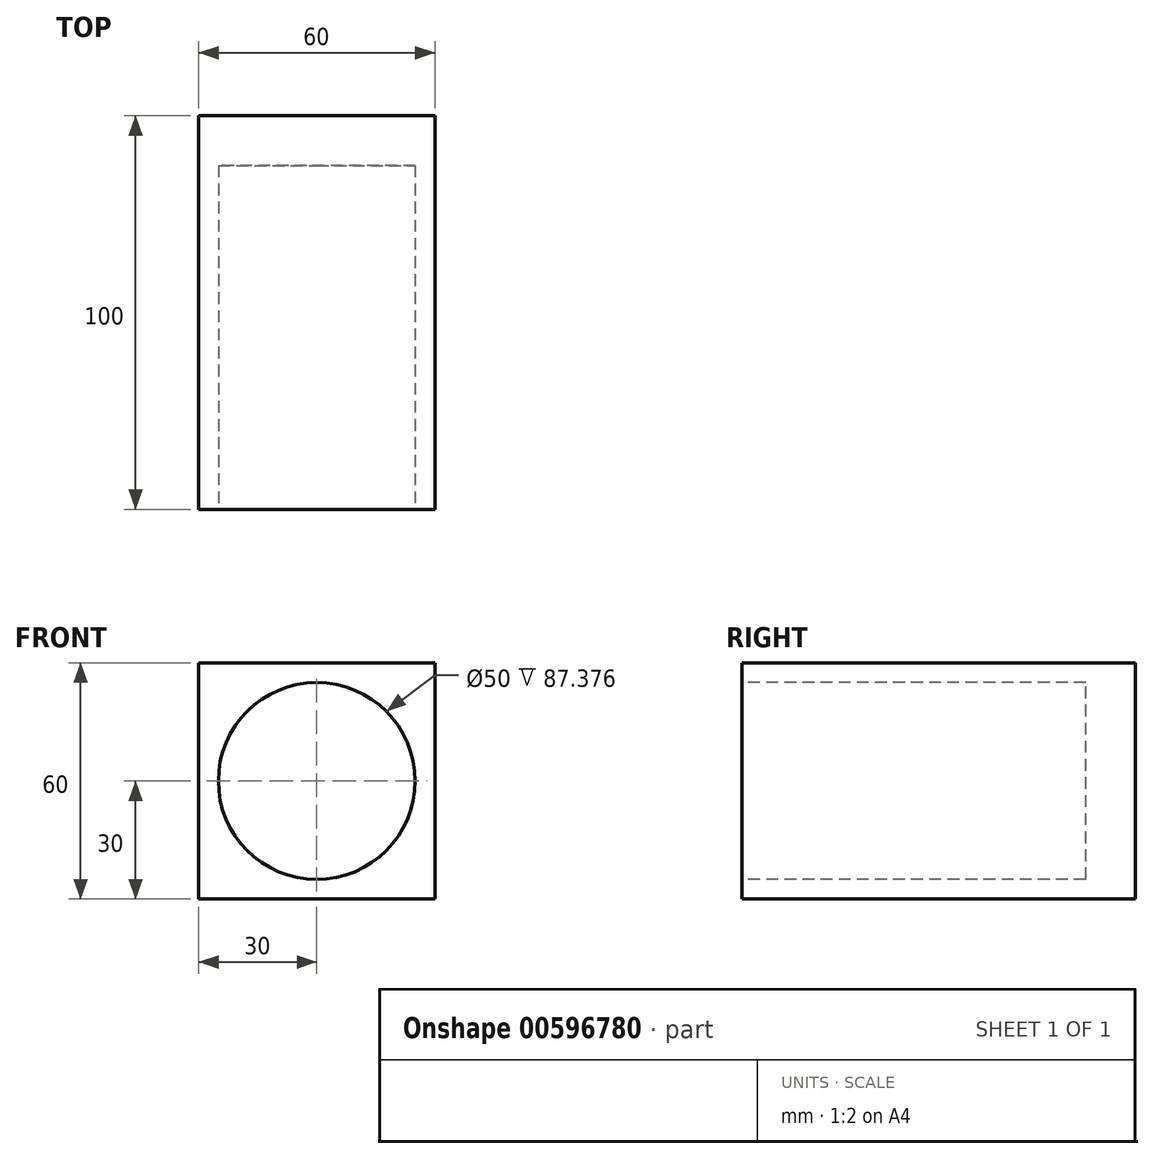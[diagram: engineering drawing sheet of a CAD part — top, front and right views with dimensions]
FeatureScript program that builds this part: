
annotation { "Feature Type Name" : "Feature", "Feature Type Description" : "" }
export const myFeature = defineFeature(function(context is Context, id is Id, definition is map)
    precondition{}
    {
        {
            var Q0;
            Q0=qCreatedBy(makeId("Front.planeOp"),FACE);
            var sketch = newSketch(context, id + "F0", { "sketchPlane" : qUnion([Q0])});
            skLineSegment(sketch, "E0.bottom", {"start": v(-30, 30) * mm, "end": v(30, 30) * mm});
            skLineSegment(sketch, "E0.top", {"start": v(-30, -30) * mm, "end": v(30, -30) * mm});
            skLineSegment(sketch, "E0.left", {"start": v(-30, 30) * mm, "end": v(-30, -30) * mm});
            skLineSegment(sketch, "E0.right", {"start": v(30, 30) * mm, "end": v(30, -30) * mm});
            skPoint(sketch, "E0.middle", {"position": v(0, 0) * mm});
            skSolve(sketch);
        }
        {
            var Q0;
            Q0=makeQuery(id+"F0.imprint","IMPRINT",FACE,{"disambiguationData":[TD([[makeQuery(id+"F0.imprint","IMPRINT",EDGE,{"derivedFrom":sQuery(id+"F0.wireOp",EDGE,"E0.bottom")}),-1.0]])]});
            extrude(context, id + "F1", {"entities" : qUnion([Q0]), "depth" : 100 * mm, "offsetDistance" : 25.4 * mm});
        }
        {
            var Q0;
            Q0=makeQuery(id+"F1.opExtrude","CAP_FACE",FACE,{"disambiguationData":[OSD([sQuery(id+"F0.wireOp",EDGE,"E0.bottom"),sQuery(id+"F0.wireOp",EDGE,"E0.top"),sQuery(id+"F0.wireOp",EDGE,"E0.left"),sQuery(id+"F0.wireOp",EDGE,"E0.right")])],"isStart":false});
            var sketch = newSketch(context, id + "F2", { "sketchPlane" : qUnion([Q0])});
            skCircle(sketch, "E1", {"center": v(0, 0) * mm, "radius": 25 * mm});
            skSolve(sketch);
        }
        {
            var Q0;
            Q0=makeQuery(id+"F2.imprint","IMPRINT",FACE,{"disambiguationData":[TD([[makeQuery(id+"F2.imprint","IMPRINT",EDGE,{"derivedFrom":sQuery(id+"F2.wireOp",EDGE,"E1")}),1.0]])]});
            extrude(context, id + "F3", {"entities" : qUnion([Q0]), "operationType" : NewBodyOperationType.REMOVE, "oppositeDirection" : true, "depth" : 87.38 * mm, "offsetDistance" : 25.4 * mm});
        }
    });
